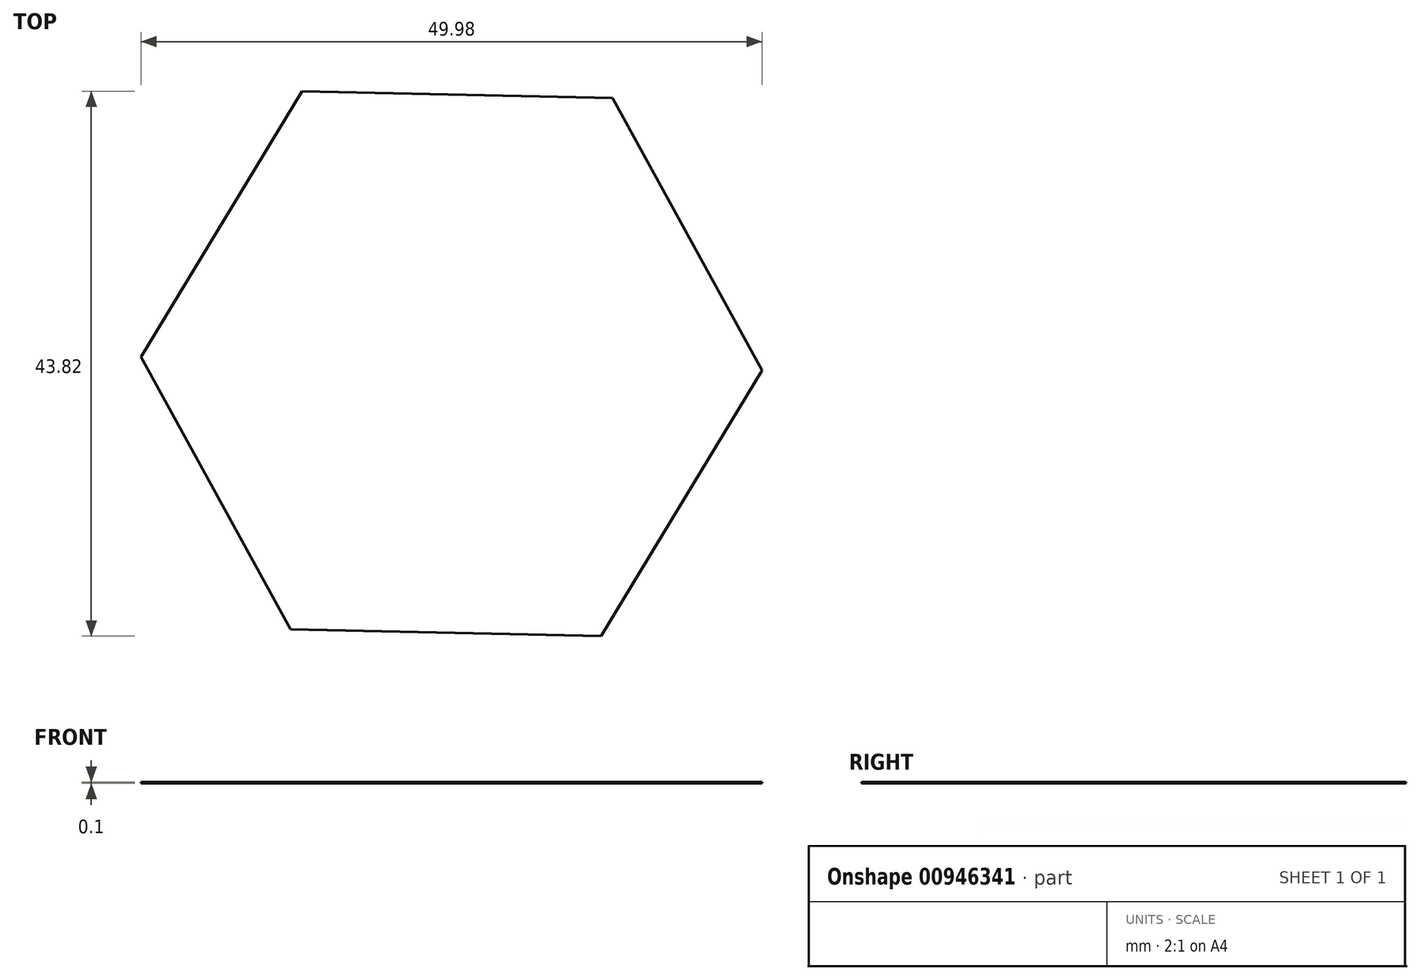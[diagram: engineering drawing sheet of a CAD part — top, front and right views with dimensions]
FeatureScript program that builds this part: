
annotation { "Feature Type Name" : "Feature", "Feature Type Description" : "" }
export const myFeature = defineFeature(function(context is Context, id is Id, definition is map)
    precondition{}
    {
        {
            var Q0;
            Q0=qCreatedBy(makeId("Top.planeOp"),FACE);
            var sketch = newSketch(context, id + "F0", { "sketchPlane" : qUnion([Q0])});
            skCircle(sketch, "E0.cCircle", {"center": v(0, 0) * mm, "radius": 21.65 * mm, "construction": true});
            skLineSegment(sketch, "E0.0", {"start": v(25, -0.53) * mm, "end": v(12.04, -21.91) * mm});
            skLineSegment(sketch, "E0.1", {"start": v(12.04, -21.91) * mm, "end": v(-12.96, -21.38) * mm});
            skLineSegment(sketch, "E0.2", {"start": v(-12.96, -21.38) * mm, "end": v(-25, 0.53) * mm});
            skLineSegment(sketch, "E0.3", {"start": v(-25, 0.53) * mm, "end": v(-12.04, 21.91) * mm});
            skLineSegment(sketch, "E0.4", {"start": v(-12.04, 21.91) * mm, "end": v(12.96, 21.38) * mm});
            skLineSegment(sketch, "E0.5", {"start": v(12.96, 21.38) * mm, "end": v(25, -0.53) * mm});
            skPoint(sketch, "E0.0.midPoint", {"position": v(18.52, -11.22) * mm});
            skSolve(sketch);
        }
        {
            var Q0;
            Q0=makeQuery(id+"F0.imprint","IMPRINT",FACE,{"disambiguationData":[TD([[makeQuery(id+"F0.imprint","IMPRINT",EDGE,{"derivedFrom":sQuery(id+"F0.wireOp",EDGE,"E0.0")}),-1.0]])]});
            extrude(context, id + "F1", {"entities" : qUnion([Q0]), "depth" : 0.1 * mm, "offsetDistance" : 25 * mm});
        }
    });
